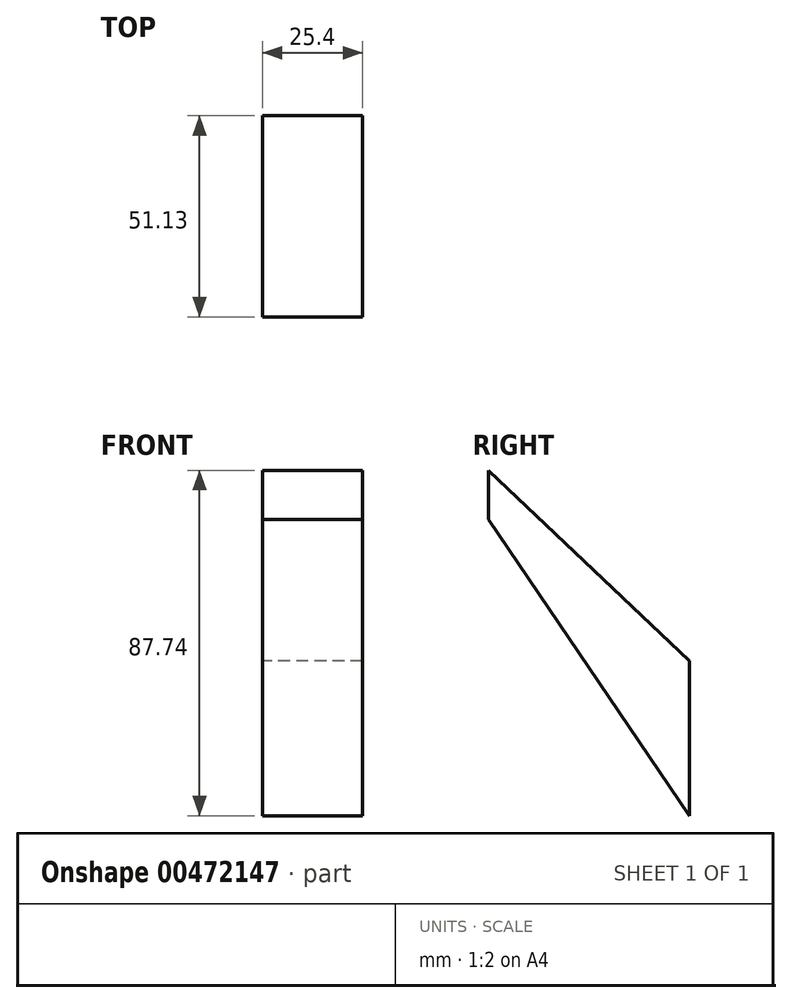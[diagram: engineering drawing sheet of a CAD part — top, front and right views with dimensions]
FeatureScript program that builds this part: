
annotation { "Feature Type Name" : "Feature", "Feature Type Description" : "" }
export const myFeature = defineFeature(function(context is Context, id is Id, definition is map)
    precondition{}
    {
        {
            var Q0;
            Q0=qCreatedBy(makeId("Right.planeOp"),FACE);
            var sketch = newSketch(context, id + "F0", { "sketchPlane" : qUnion([Q0])});
            skLineSegment(sketch, "E0", {"start": v(-69.72, 137.24) * mm, "end": v(-18.6, 88.8) * mm});
            skLineSegment(sketch, "E1", {"start": v(-18.6, 88.8) * mm, "end": v(-18.6, 49.5) * mm});
            skLineSegment(sketch, "E2", {"start": v(-18.6, 49.5) * mm, "end": v(-69.72, 124.75) * mm});
            skLineSegment(sketch, "E3", {"start": v(-69.72, 124.75) * mm, "end": v(-69.72, 137.24) * mm});
            skSolve(sketch);
        }
        {
            var Q0;
            Q0=makeQuery(id+"F0.imprint","IMPRINT",FACE,{"disambiguationData":[TD([[makeQuery(id+"F0.imprint","IMPRINT",EDGE,{"derivedFrom":sQuery(id+"F0.wireOp",EDGE,"E0")}),-1.0]])]});
            extrude(context, id + "F1", {"entities" : qUnion([Q0]), "depth" : 25.4 * mm});
        }
    });
